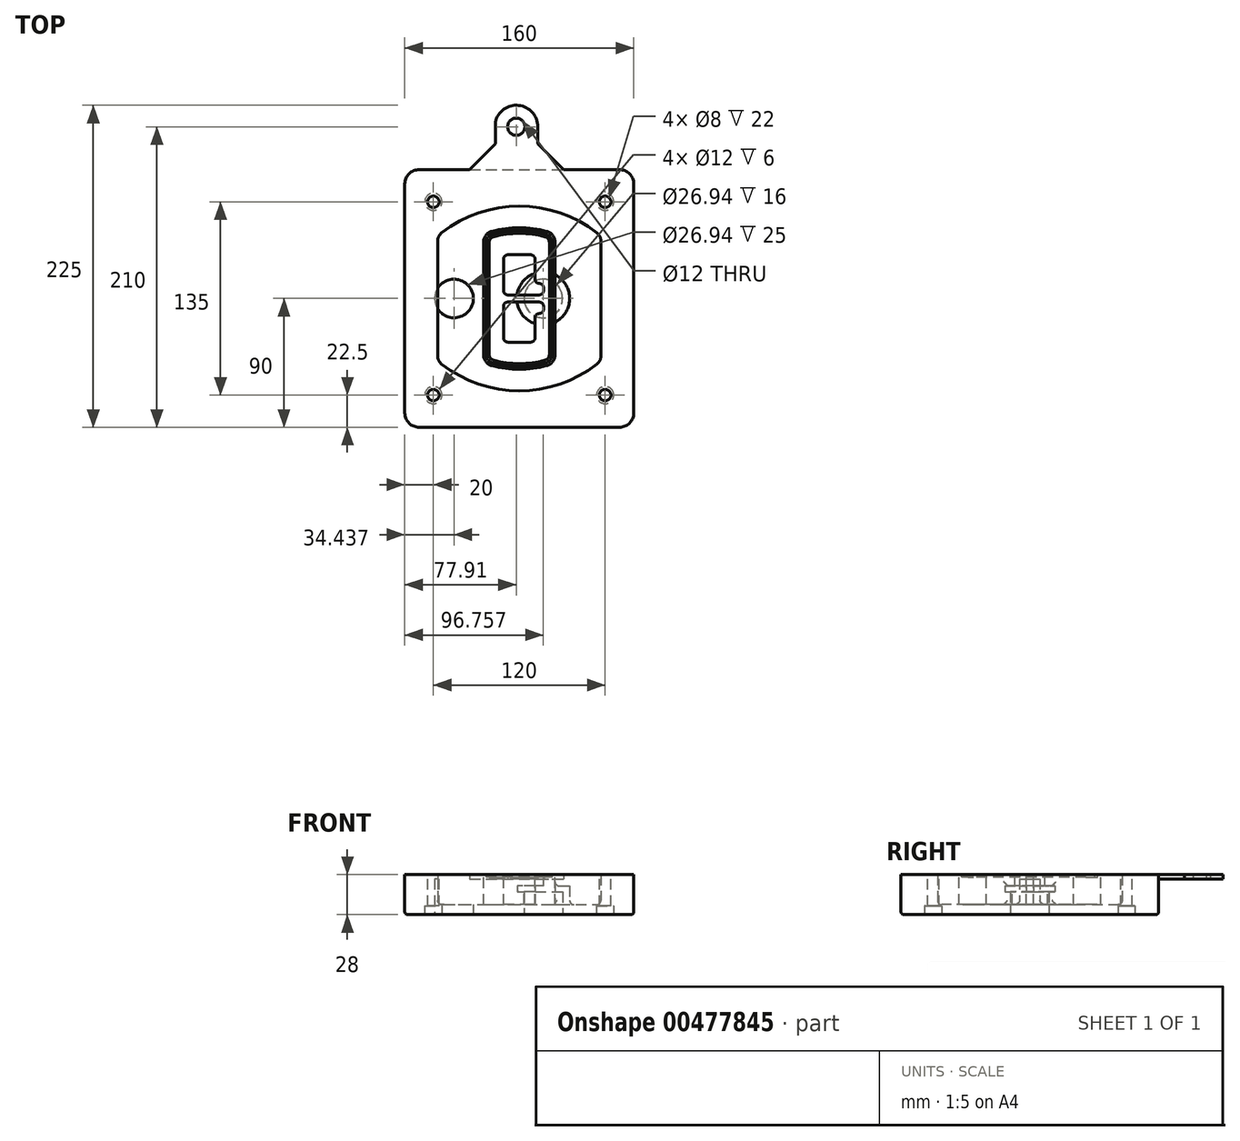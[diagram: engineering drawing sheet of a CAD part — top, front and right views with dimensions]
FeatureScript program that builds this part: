
annotation { "Feature Type Name" : "Feature", "Feature Type Description" : "" }
export const myFeature = defineFeature(function(context is Context, id is Id, definition is map)
    precondition{}
    {
        {
            var Q0;
            Q0=qCreatedBy(makeId("Top.planeOp"),FACE);
            var sketch = newSketch(context, id + "F0", { "sketchPlane" : qUnion([Q0])});
            skPoint(sketch, "E0.rect.middle", {"position": v(0, 0) * mm});
            skLineSegment(sketch, "E1.bottom", {"start": v(-70, -90) * mm, "end": v(70, -90) * mm});
            skLineSegment(sketch, "E1.top", {"start": v(-70, 90) * mm, "end": v(70, 90) * mm});
            skLineSegment(sketch, "E1.left", {"start": v(-80, -80) * mm, "end": v(-80, 80) * mm});
            skLineSegment(sketch, "E1.right", {"start": v(80, -80) * mm, "end": v(80, 80) * mm});
            skLineSegment(sketch, "E2", {"start": v(-80, 90) * mm, "end": v(80, -90) * mm, "construction": true});
            skLineSegment(sketch, "E3", {"start": v(80, 90) * mm, "end": v(-80, -90) * mm, "construction": true});
            skCircle(sketch, "E4", {"center": v(-60, 67.5) * mm, "radius": 4 * mm});
            skCircle(sketch, "E5", {"center": v(60, 67.5) * mm, "radius": 4 * mm});
            skCircle(sketch, "E6", {"center": v(60, -67.5) * mm, "radius": 4 * mm});
            skCircle(sketch, "E7", {"center": v(-60, -67.5) * mm, "radius": 4 * mm});
            skLineSegment(sketch, "E8", {"start": v(-60, 67.5) * mm, "end": v(60, 67.5) * mm, "construction": true});
            skLineSegment(sketch, "E9", {"start": v(60, 67.5) * mm, "end": v(60, -67.5) * mm, "construction": true});
            skLineSegment(sketch, "E10", {"start": v(60, -67.5) * mm, "end": v(-60, -67.5) * mm, "construction": true});
            skLineSegment(sketch, "E11", {"start": v(-60, -67.5) * mm, "end": v(-60, 67.5) * mm, "construction": true});
            skLineSegment(sketch, "E12", {"start": v(-60, 40.3) * mm, "end": v(-60, -40.3) * mm});
            skLineSegment(sketch, "E13", {"start": v(60, 40.3) * mm, "end": v(60, -40.3) * mm});
            skArc(sketch, "E14", {"start": v(56.15, 48.18) * mm, "mid": v(0, 67.5) * mm, "end": v(-56.15, 48.18) * mm});
            skArc(sketch, "E15", {"start": v(-56.15, -48.18) * mm, "mid": v(0, -67.5) * mm, "end": v(56.15, -48.18) * mm});
            skLineSegment(sketch, "E16", {"start": v(-60, 0) * mm, "end": v(60, 0) * mm, "construction": true});
            skPoint(sketch, "E17.visualSharp", {"position": v(-60, -45) * mm});
            skArc(sketch, "E17.filletArc", {"start": v(-60, -40.3) * mm, "mid": v(-58.99, -44.68) * mm, "end": v(-56.15, -48.18) * mm});
            skPoint(sketch, "E18.visualSharp", {"position": v(-60, 45) * mm});
            skArc(sketch, "E18.filletArc", {"start": v(-56.15, 48.18) * mm, "mid": v(-58.99, 44.68) * mm, "end": v(-60, 40.3) * mm});
            skPoint(sketch, "E19.visualSharp", {"position": v(60, 45) * mm});
            skArc(sketch, "E19.filletArc", {"start": v(60, 40.3) * mm, "mid": v(58.99, 44.68) * mm, "end": v(56.15, 48.18) * mm});
            skPoint(sketch, "E20.visualSharp", {"position": v(60, -45) * mm});
            skArc(sketch, "E20.filletArc", {"start": v(56.15, -48.18) * mm, "mid": v(58.99, -44.68) * mm, "end": v(60, -40.3) * mm});
            skPoint(sketch, "E21.visualSharp", {"position": v(-80, 90) * mm});
            skArc(sketch, "E21.filletArc", {"start": v(-70, 90) * mm, "mid": v(-77.07, 87.07) * mm, "end": v(-80, 80) * mm});
            skPoint(sketch, "E22.visualSharp", {"position": v(80, 90) * mm});
            skArc(sketch, "E22.filletArc", {"start": v(80, 80) * mm, "mid": v(77.07, 87.07) * mm, "end": v(70, 90) * mm});
            skPoint(sketch, "E23.visualSharp", {"position": v(80, -90) * mm});
            skArc(sketch, "E23.filletArc", {"start": v(70, -90) * mm, "mid": v(77.07, -87.07) * mm, "end": v(80, -80) * mm});
            skPoint(sketch, "E24.visualSharp", {"position": v(-80, -90) * mm});
            skArc(sketch, "E24.filletArc", {"start": v(-80, -80) * mm, "mid": v(-77.07, -87.07) * mm, "end": v(-70, -90) * mm});
            skArc(sketch, "E25.0", {"start": v(57, 40.3) * mm, "mid": v(56.3, 43.36) * mm, "end": v(54.3, 45.81) * mm});
            skLineSegment(sketch, "E25.1", {"start": v(57, 40.3) * mm, "end": v(57, -40.3) * mm});
            skArc(sketch, "E25.2", {"start": v(54.3, -45.81) * mm, "mid": v(56.3, -43.36) * mm, "end": v(57, -40.3) * mm});
            skArc(sketch, "E25.3", {"start": v(-54.3, -45.81) * mm, "mid": v(0, -64.5) * mm, "end": v(54.3, -45.81) * mm});
            skArc(sketch, "E25.4", {"start": v(-57, -40.3) * mm, "mid": v(-56.3, -43.36) * mm, "end": v(-54.3, -45.81) * mm});
            skArc(sketch, "E25.5", {"start": v(54.3, 45.81) * mm, "mid": v(0, 64.5) * mm, "end": v(-54.3, 45.81) * mm});
            skLineSegment(sketch, "E25.6", {"start": v(-57, 40.3) * mm, "end": v(-57, -40.3) * mm});
            skArc(sketch, "E25.7", {"start": v(-54.3, 45.81) * mm, "mid": v(-56.3, 43.36) * mm, "end": v(-57, 40.3) * mm});
            skArc(sketch, "E26.0", {"start": v(-58.62, 51.33) * mm, "mid": v(-62.58, 46.43) * mm, "end": v(-64, 40.3) * mm});
            skArc(sketch, "E26.1", {"start": v(58.62, 51.33) * mm, "mid": v(0, 71.5) * mm, "end": v(-58.62, 51.33) * mm});
            skArc(sketch, "E26.2", {"start": v(64, 40.3) * mm, "mid": v(62.58, 46.43) * mm, "end": v(58.62, 51.33) * mm});
            skLineSegment(sketch, "E26.3", {"start": v(64, 40.3) * mm, "end": v(64, -40.3) * mm});
            skArc(sketch, "E26.4", {"start": v(58.62, -51.33) * mm, "mid": v(62.58, -46.43) * mm, "end": v(64, -40.3) * mm});
            skLineSegment(sketch, "E26.5", {"start": v(-64, 40.3) * mm, "end": v(-64, -40.3) * mm});
            skArc(sketch, "E26.6", {"start": v(-58.62, -51.33) * mm, "mid": v(0, -71.5) * mm, "end": v(58.62, -51.33) * mm});
            skArc(sketch, "E26.7", {"start": v(-64, -40.3) * mm, "mid": v(-62.58, -46.43) * mm, "end": v(-58.62, -51.33) * mm});
            skSolve(sketch);
        }
        {
            var Q0;
            Q0=makeQuery(id+"F0.imprint","IMPRINT",FACE,{"disambiguationData":[TD([[makeQuery(id+"F0.imprint","IMPRINT",EDGE,{"derivedFrom":sQuery(id+"F0.wireOp",EDGE,"E1.bottom")}),1.0]])]});
            var Q1;
            Q1=makeQuery(id+"F0.imprint","IMPRINT",FACE,{"disambiguationData":[TD([[makeQuery(id+"F0.imprint","IMPRINT",EDGE,{"derivedFrom":sQuery(id+"F0.wireOp",EDGE,"E12")}),1.0]])]});
            var Q2;
            Q2=makeQuery(id+"F0.imprint","IMPRINT",FACE,{"disambiguationData":[TD([[makeQuery(id+"F0.imprint","IMPRINT",EDGE,{"derivedFrom":sQuery(id+"F0.wireOp",EDGE,"E25.0")}),1.0]])]});
            var Q3;
            Q3=makeQuery(id+"F0.imprint","IMPRINT",FACE,{"disambiguationData":[TD([[makeQuery(id+"F0.imprint","IMPRINT",EDGE,{"derivedFrom":sQuery(id+"F0.wireOp",EDGE,"E12")}),-1.0]])]});
            extrude(context, id + "F1", {"entities" : qUnion([Q0, Q1, Q2, Q3]), "oppositeDirection" : true, "depth" : 25 * mm});
        }
        {
            var Q0;
            Q0=makeQuery(id+"F0.imprint","IMPRINT",FACE,{"disambiguationData":[TD([[makeQuery(id+"F0.imprint","IMPRINT",EDGE,{"derivedFrom":sQuery(id+"F0.wireOp",EDGE,"E12")}),1.0]])]});
            extrude(context, id + "F2", {"entities" : qUnion([Q0]), "operationType" : NewBodyOperationType.ADD, "depth" : 3 * mm});
        }
        {
            var Q0;
            Q0=makeQuery(id+"F0.imprint","IMPRINT",FACE,{"disambiguationData":[TD([[makeQuery(id+"F0.imprint","IMPRINT",EDGE,{"derivedFrom":sQuery(id+"F0.wireOp",EDGE,"E25.0")}),1.0]])]});
            extrude(context, id + "F3", {"entities" : qUnion([Q0]), "operationType" : NewBodyOperationType.REMOVE, "oppositeDirection" : true, "depth" : 18 * mm});
        }
        {
            var Q0;
            Q0=makeQuery(id+"F2.opExtrude","CAP_FACE",FACE,{"disambiguationData":[OSD([sQuery(id+"F0.wireOp",EDGE,"E12"),sQuery(id+"F0.wireOp",EDGE,"E13"),sQuery(id+"F0.wireOp",EDGE,"E14"),sQuery(id+"F0.wireOp",EDGE,"E15"),sQuery(id+"F0.wireOp",EDGE,"E17.filletArc"),sQuery(id+"F0.wireOp",EDGE,"E18.filletArc"),sQuery(id+"F0.wireOp",EDGE,"E19.filletArc"),sQuery(id+"F0.wireOp",EDGE,"E20.filletArc"),sQuery(id+"F0.wireOp",EDGE,"E25.0"),sQuery(id+"F0.wireOp",EDGE,"E25.1"),sQuery(id+"F0.wireOp",EDGE,"E25.2"),sQuery(id+"F0.wireOp",EDGE,"E25.3"),sQuery(id+"F0.wireOp",EDGE,"E25.4"),sQuery(id+"F0.wireOp",EDGE,"E25.5"),sQuery(id+"F0.wireOp",EDGE,"E25.6"),sQuery(id+"F0.wireOp",EDGE,"E25.7")])],"isStart":false});
            var sketch = newSketch(context, id + "F4", { "sketchPlane" : qUnion([Q0])});
            skArc(sketch, "E27.0", {"start": v(-19.08, -46.97) * mm, "mid": v(0, -49.5) * mm, "end": v(19.08, -46.97) * mm});
            skArc(sketch, "E28.0", {"start": v(19.08, 46.97) * mm, "mid": v(0, 49.5) * mm, "end": v(-19.08, 46.97) * mm});
            skLineSegment(sketch, "E29", {"start": v(-25, 39.25) * mm, "end": v(-25, -39.25) * mm});
            skLineSegment(sketch, "E30", {"start": v(25, 39.25) * mm, "end": v(25, -39.25) * mm});
            skLineSegment(sketch, "E31", {"start": v(-25, 45.1) * mm, "end": v(25, 45.1) * mm, "construction": true});
            skLineSegment(sketch, "E32", {"start": v(-25, -45.1) * mm, "end": v(25, -45.1) * mm, "construction": true});
            skPoint(sketch, "E33.visualSharp", {"position": v(-25, 45.1) * mm});
            skArc(sketch, "E33.filletArc", {"start": v(-19.08, 46.97) * mm, "mid": v(-23.35, 44.11) * mm, "end": v(-25, 39.25) * mm});
            skPoint(sketch, "E34.visualSharp", {"position": v(25, 45.1) * mm});
            skArc(sketch, "E34.filletArc", {"start": v(25, 39.25) * mm, "mid": v(23.35, 44.11) * mm, "end": v(19.08, 46.97) * mm});
            skPoint(sketch, "E35.visualSharp", {"position": v(25, -45.1) * mm});
            skArc(sketch, "E35.filletArc", {"start": v(19.08, -46.97) * mm, "mid": v(23.35, -44.11) * mm, "end": v(25, -39.25) * mm});
            skPoint(sketch, "E36.visualSharp", {"position": v(-25, -45.1) * mm});
            skArc(sketch, "E36.filletArc", {"start": v(-25, -39.25) * mm, "mid": v(-23.35, -44.11) * mm, "end": v(-19.08, -46.97) * mm});
            skArc(sketch, "E37.0", {"start": v(54.3, 45.81) * mm, "mid": v(0, 64.5) * mm, "end": v(-54.3, 45.81) * mm});
            skArc(sketch, "E37.1", {"start": v(-54.3, 45.81) * mm, "mid": v(-56.3, 43.36) * mm, "end": v(-57, 40.3) * mm});
            skLineSegment(sketch, "E37.2", {"start": v(-57, 40.3) * mm, "end": v(-57, -40.3) * mm});
            skArc(sketch, "E37.3", {"start": v(-57, -40.3) * mm, "mid": v(-56.3, -43.36) * mm, "end": v(-54.3, -45.81) * mm});
            skArc(sketch, "E37.4", {"start": v(-54.3, -45.81) * mm, "mid": v(0, -64.5) * mm, "end": v(54.3, -45.81) * mm});
            skArc(sketch, "E37.5", {"start": v(54.3, -45.81) * mm, "mid": v(56.3, -43.36) * mm, "end": v(57, -40.3) * mm});
            skLineSegment(sketch, "E37.6", {"start": v(57, 40.3) * mm, "end": v(57, -40.3) * mm});
            skArc(sketch, "E37.7", {"start": v(57, 40.3) * mm, "mid": v(56.3, 43.36) * mm, "end": v(54.3, 45.81) * mm});
            skLineSegment(sketch, "E38.0", {"start": v(23, 39.25) * mm, "end": v(23, -39.25) * mm});
            skArc(sketch, "E38.1", {"start": v(18.56, -45.04) * mm, "mid": v(21.76, -42.9) * mm, "end": v(23, -39.25) * mm});
            skArc(sketch, "E38.2", {"start": v(-18.56, -45.04) * mm, "mid": v(0, -47.5) * mm, "end": v(18.56, -45.04) * mm});
            skArc(sketch, "E38.3", {"start": v(-23, -39.25) * mm, "mid": v(-21.76, -42.9) * mm, "end": v(-18.56, -45.04) * mm});
            skLineSegment(sketch, "E38.4", {"start": v(-23, 39.25) * mm, "end": v(-23, -39.25) * mm});
            skArc(sketch, "E38.5", {"start": v(23, 39.25) * mm, "mid": v(21.76, 42.9) * mm, "end": v(18.56, 45.04) * mm});
            skArc(sketch, "E38.6", {"start": v(-18.56, 45.04) * mm, "mid": v(-21.76, 42.9) * mm, "end": v(-23, 39.25) * mm});
            skArc(sketch, "E38.7", {"start": v(18.56, 45.04) * mm, "mid": v(0, 47.5) * mm, "end": v(-18.56, 45.04) * mm});
            skArc(sketch, "E39.0", {"start": v(21, 39.25) * mm, "mid": v(20.18, 41.68) * mm, "end": v(18.04, 43.1) * mm});
            skLineSegment(sketch, "E39.1", {"start": v(21, 39.25) * mm, "end": v(21, -39.25) * mm});
            skArc(sketch, "E39.2", {"start": v(18.04, -43.1) * mm, "mid": v(20.18, -41.68) * mm, "end": v(21, -39.25) * mm});
            skArc(sketch, "E39.3", {"start": v(-18.04, -43.1) * mm, "mid": v(0, -45.5) * mm, "end": v(18.04, -43.1) * mm});
            skArc(sketch, "E39.4", {"start": v(-21, -39.25) * mm, "mid": v(-20.18, -41.68) * mm, "end": v(-18.04, -43.1) * mm});
            skArc(sketch, "E39.5", {"start": v(18.04, 43.1) * mm, "mid": v(0, 45.5) * mm, "end": v(-18.04, 43.1) * mm});
            skLineSegment(sketch, "E39.6", {"start": v(-21, 39.25) * mm, "end": v(-21, -39.25) * mm});
            skArc(sketch, "E39.7", {"start": v(-18.04, 43.1) * mm, "mid": v(-20.18, 41.68) * mm, "end": v(-21, 39.25) * mm});
            skLineSegment(sketch, "E40", {"start": v(-25, 0) * mm, "end": v(25, 0) * mm, "construction": true});
            skLineSegment(sketch, "E41", {"start": v(-11, 5.5) * mm, "end": v(-11, 27.5) * mm});
            skLineSegment(sketch, "E42", {"start": v(-8, 30.5) * mm, "end": v(8, 30.5) * mm});
            skLineSegment(sketch, "E43", {"start": v(11, 27.5) * mm, "end": v(11, 13.5) * mm});
            skLineSegment(sketch, "E44", {"start": v(14, 10.5) * mm, "end": v(14, 10.5) * mm});
            skLineSegment(sketch, "E45", {"start": v(17, 7.5) * mm, "end": v(17, 5.5) * mm});
            skLineSegment(sketch, "E46", {"start": v(14, 2.5) * mm, "end": v(-8, 2.5) * mm});
            skPoint(sketch, "E47.visualSharp", {"position": v(-11, 30.5) * mm});
            skArc(sketch, "E47.filletArc", {"start": v(-8, 30.5) * mm, "mid": v(-10.12, 29.62) * mm, "end": v(-11, 27.5) * mm});
            skPoint(sketch, "E48.visualSharp", {"position": v(11, 30.5) * mm});
            skArc(sketch, "E48.filletArc", {"start": v(11, 27.5) * mm, "mid": v(10.12, 29.62) * mm, "end": v(8, 30.5) * mm});
            skPoint(sketch, "E49.visualSharp", {"position": v(11, 10.5) * mm});
            skArc(sketch, "E49.filletArc", {"start": v(11, 13.5) * mm, "mid": v(11.88, 11.38) * mm, "end": v(14, 10.5) * mm});
            skPoint(sketch, "E50.visualSharp", {"position": v(17, 10.5) * mm});
            skArc(sketch, "E50.filletArc", {"start": v(17, 7.5) * mm, "mid": v(16.12, 9.62) * mm, "end": v(14, 10.5) * mm});
            skPoint(sketch, "E51.visualSharp", {"position": v(17, 2.5) * mm});
            skArc(sketch, "E51.filletArc", {"start": v(14, 2.5) * mm, "mid": v(16.12, 3.38) * mm, "end": v(17, 5.5) * mm});
            skPoint(sketch, "E52.visualSharp", {"position": v(-11, 2.5) * mm});
            skArc(sketch, "E52.filletArc", {"start": v(-11, 5.5) * mm, "mid": v(-10.12, 3.38) * mm, "end": v(-8, 2.5) * mm});
            skLineSegment(sketch, "E53.0.MirrorCS", {"start": v(14, -2.5) * mm, "end": v(-8, -2.5) * mm});
            skArc(sketch, "E54.0.MirrorCS", {"start": v(-11, -5.5) * mm, "mid": v(-10.12, -3.38) * mm, "end": v(-8, -2.5) * mm});
            skLineSegment(sketch, "E55.0.MirrorCS", {"start": v(-11, -5.5) * mm, "end": v(-11, -27.5) * mm});
            skArc(sketch, "E56.0.MirrorCS", {"start": v(-8, -30.5) * mm, "mid": v(-10.12, -29.62) * mm, "end": v(-11, -27.5) * mm});
            skLineSegment(sketch, "E57.0.MirrorCS", {"start": v(-8, -30.5) * mm, "end": v(8, -30.5) * mm});
            skArc(sketch, "E58.0.MirrorCS", {"start": v(11, -27.5) * mm, "mid": v(10.12, -29.62) * mm, "end": v(8, -30.5) * mm});
            skLineSegment(sketch, "E59.0.MirrorCS", {"start": v(11, -27.5) * mm, "end": v(11, -13.5) * mm});
            skArc(sketch, "E60.0.MirrorCS", {"start": v(11, -13.5) * mm, "mid": v(11.88, -11.38) * mm, "end": v(14, -10.5) * mm});
            skArc(sketch, "E61.0.MirrorCS", {"start": v(17, -7.5) * mm, "mid": v(16.12, -9.62) * mm, "end": v(14, -10.5) * mm});
            skLineSegment(sketch, "E62.0.MirrorCS", {"start": v(17, -7.5) * mm, "end": v(17, -5.5) * mm});
            skArc(sketch, "E63.0.MirrorCS", {"start": v(14, -2.5) * mm, "mid": v(16.12, -3.38) * mm, "end": v(17, -5.5) * mm});
            skSolve(sketch);
        }
        {
            var Q0;
            Q0=makeQuery(id+"F4.imprint","IMPRINT",FACE,{"disambiguationData":[TD([[makeQuery(id+"F4.imprint","IMPRINT",EDGE,{"derivedFrom":sQuery(id+"F4.wireOp",EDGE,"E27.0")}),1.0]])]});
            var Q1;
            Q1=makeQuery(id+"F4.imprint","IMPRINT",FACE,{"disambiguationData":[TD([[makeQuery(id+"F4.imprint","IMPRINT",EDGE,{"derivedFrom":sQuery(id+"F4.wireOp",EDGE,"E38.0")}),-1.0]])]});
            var Q2;
            Q2=makeQuery(id+"F4.imprint","IMPRINT",FACE,{"disambiguationData":[TD([[makeQuery(id+"F4.imprint","IMPRINT",EDGE,{"derivedFrom":sQuery(id+"F4.wireOp",EDGE,"E39.0")}),1.0]])]});
            extrude(context, id + "F5", {"entities" : qUnion([Q0, Q1, Q2]), "operationType" : NewBodyOperationType.ADD, "endBound" : BoundingType.UP_TO_NEXT, "oppositeDirection" : true, "depth" : 25 * mm});
        }
        {
            var Q0;
            Q0=makeQuery(id+"F4.imprint","IMPRINT",FACE,{"disambiguationData":[TD([[makeQuery(id+"F4.imprint","IMPRINT",EDGE,{"derivedFrom":sQuery(id+"F4.wireOp",EDGE,"E38.0")}),-1.0]])]});
            extrude(context, id + "F6", {"entities" : qUnion([Q0]), "operationType" : NewBodyOperationType.REMOVE, "oppositeDirection" : true, "depth" : 2 * mm});
        }
        {
            var Q0;
            Q0=makeQuery(id+"F1.opExtrude","CAP_FACE",FACE,{"disambiguationData":[OSD([sQuery(id+"F0.wireOp",EDGE,"E1.bottom"),sQuery(id+"F0.wireOp",EDGE,"E1.top"),sQuery(id+"F0.wireOp",EDGE,"E1.left"),sQuery(id+"F0.wireOp",EDGE,"E1.right"),sQuery(id+"F0.wireOp",EDGE,"E4"),sQuery(id+"F0.wireOp",EDGE,"E5"),sQuery(id+"F0.wireOp",EDGE,"E6"),sQuery(id+"F0.wireOp",EDGE,"E7"),sQuery(id+"F0.wireOp",EDGE,"E21.filletArc"),sQuery(id+"F0.wireOp",EDGE,"E22.filletArc"),sQuery(id+"F0.wireOp",EDGE,"E23.filletArc"),sQuery(id+"F0.wireOp",EDGE,"E24.filletArc")])],"isStart":false});
            var sketch = newSketch(context, id + "F7", { "sketchPlane" : qUnion([Q0])});
            skCircle(sketch, "E64", {"center": v(16.76, 0) * mm, "radius": 13.47 * mm});
            skCircle(sketch, "E65", {"center": v(-45.56, 0) * mm, "radius": 13.47 * mm});
            skLineSegment(sketch, "E66", {"start": v(80, 0) * mm, "end": v(-80, 0) * mm});
            skCircle(sketch, "E67", {"center": v(16.76, 0) * mm, "radius": 18.47 * mm});
            skCircle(sketch, "E68", {"center": v(60, -67.5) * mm, "radius": 6 * mm});
            skCircle(sketch, "E69", {"center": v(-60, -67.5) * mm, "radius": 6 * mm});
            skCircle(sketch, "E70", {"center": v(-60, 67.5) * mm, "radius": 6 * mm});
            skCircle(sketch, "E71", {"center": v(60, 67.5) * mm, "radius": 6 * mm});
            skSolve(sketch);
        }
        {
            var Q0;
            {var subQ1=sQuery(id+"F7.wireOp",EDGE,"E66");var subQ4=sQuery(id+"F7.wireOp",EDGE,"E64");var subQ6=makeQuery(id+"F7.imprint","INTERSECT",VERTEX,{"disambiguationData":[OD(0.0)],"derivedFrom":[subQ4,subQ1]});Q0=makeQuery(id+"F7.imprint","IMPRINT",FACE,{"disambiguationData":[TD([[makeQuery(id+"F7.imprint","IMPRINT",EDGE,{"disambiguationData":[TD([[subQ6,-1.0]])],"derivedFrom":subQ4}),-1.0]])]});}
            var Q1;
            {var subQ0=sQuery(id+"F7.wireOp",EDGE,"E66");var subQ1=sQuery(id+"F7.wireOp",EDGE,"E64");var subQ3=makeQuery(id+"F7.imprint","INTERSECT",VERTEX,{"disambiguationData":[OD(0.0)],"derivedFrom":[subQ1,subQ0]});Q1=makeQuery(id+"F7.imprint","IMPRINT",FACE,{"disambiguationData":[TD([[makeQuery(id+"F7.imprint","IMPRINT",EDGE,{"disambiguationData":[TD([[subQ3,-1.0]])],"derivedFrom":subQ1}),1.0]])]});}
            var Q2;
            {var subQ0=sQuery(id+"F7.wireOp",EDGE,"E66");var subQ1=sQuery(id+"F7.wireOp",EDGE,"E64");var subQ3=makeQuery(id+"F7.imprint","INTERSECT",VERTEX,{"disambiguationData":[OD(0.0)],"derivedFrom":[subQ1,subQ0]});Q2=makeQuery(id+"F7.imprint","IMPRINT",FACE,{"disambiguationData":[TD([[makeQuery(id+"F7.imprint","IMPRINT",EDGE,{"disambiguationData":[TD([[subQ3,1.0]])],"derivedFrom":subQ1}),1.0]])]});}
            var Q3;
            {var subQ1=sQuery(id+"F7.wireOp",EDGE,"E66");var subQ4=sQuery(id+"F7.wireOp",EDGE,"E64");var subQ6=makeQuery(id+"F7.imprint","INTERSECT",VERTEX,{"disambiguationData":[OD(0.0)],"derivedFrom":[subQ4,subQ1]});Q3=makeQuery(id+"F7.imprint","IMPRINT",FACE,{"disambiguationData":[TD([[makeQuery(id+"F7.imprint","IMPRINT",EDGE,{"disambiguationData":[TD([[subQ6,1.0]])],"derivedFrom":subQ4}),-1.0]])]});}
            extrude(context, id + "F8", {"entities" : qUnion([Q0, Q1, Q2, Q3]), "operationType" : NewBodyOperationType.ADD, "oppositeDirection" : true, "depth" : 20 * mm});
        }
        {
            var Q0;
            {var subQ0=sQuery(id+"F7.wireOp",EDGE,"E66");var subQ1=sQuery(id+"F7.wireOp",EDGE,"E64");var subQ3=makeQuery(id+"F7.imprint","INTERSECT",VERTEX,{"disambiguationData":[OD(0.0)],"derivedFrom":[subQ1,subQ0]});Q0=makeQuery(id+"F7.imprint","IMPRINT",FACE,{"disambiguationData":[TD([[makeQuery(id+"F7.imprint","IMPRINT",EDGE,{"disambiguationData":[TD([[subQ3,-1.0]])],"derivedFrom":subQ1}),1.0]])]});}
            var Q1;
            {var subQ0=sQuery(id+"F7.wireOp",EDGE,"E66");var subQ1=sQuery(id+"F7.wireOp",EDGE,"E64");var subQ3=makeQuery(id+"F7.imprint","INTERSECT",VERTEX,{"disambiguationData":[OD(0.0)],"derivedFrom":[subQ1,subQ0]});Q1=makeQuery(id+"F7.imprint","IMPRINT",FACE,{"disambiguationData":[TD([[makeQuery(id+"F7.imprint","IMPRINT",EDGE,{"disambiguationData":[TD([[subQ3,1.0]])],"derivedFrom":subQ1}),1.0]])]});}
            extrude(context, id + "F9", {"entities" : qUnion([Q0, Q1]), "operationType" : NewBodyOperationType.REMOVE, "oppositeDirection" : true, "depth" : 16 * mm});
        }
        {
            var Q0;
            {var subQ0=sQuery(id+"F7.wireOp",EDGE,"E66");var subQ1=sQuery(id+"F7.wireOp",EDGE,"E65");var subQ3=makeQuery(id+"F7.imprint","INTERSECT",VERTEX,{"disambiguationData":[OD(0.0)],"derivedFrom":[subQ1,subQ0]});Q0=makeQuery(id+"F7.imprint","IMPRINT",FACE,{"disambiguationData":[TD([[makeQuery(id+"F7.imprint","IMPRINT",EDGE,{"disambiguationData":[TD([[subQ3,-1.0]])],"derivedFrom":subQ1}),1.0]])]});}
            var Q1;
            {var subQ0=sQuery(id+"F7.wireOp",EDGE,"E66");var subQ1=sQuery(id+"F7.wireOp",EDGE,"E65");var subQ3=makeQuery(id+"F7.imprint","INTERSECT",VERTEX,{"disambiguationData":[OD(0.0)],"derivedFrom":[subQ1,subQ0]});Q1=makeQuery(id+"F7.imprint","IMPRINT",FACE,{"disambiguationData":[TD([[makeQuery(id+"F7.imprint","IMPRINT",EDGE,{"disambiguationData":[TD([[subQ3,1.0]])],"derivedFrom":subQ1}),1.0]])]});}
            extrude(context, id + "F10", {"entities" : qUnion([Q0, Q1]), "operationType" : NewBodyOperationType.REMOVE, "oppositeDirection" : true, "depth" : 25 * mm});
        }
        {
            var Q0;
            Q0=makeQuery(id+"F7.imprint","IMPRINT",FACE,{"disambiguationData":[TD([[makeQuery(id+"F7.imprint","IMPRINT",EDGE,{"derivedFrom":sQuery(id+"F7.wireOp",EDGE,"E68")}),1.0]])]});
            var Q1;
            Q1=makeQuery(id+"F7.imprint","IMPRINT",FACE,{"disambiguationData":[TD([[makeQuery(id+"F7.imprint","IMPRINT",EDGE,{"derivedFrom":makeQuery(id+"F1.opExtrude","CAP_EDGE",EDGE,{"disambiguationData":[OSD([sQuery(id+"F0.wireOp",EDGE,"E5")])],"isStart":false})}),-1.0]])]});
            var Q2;
            Q2=makeQuery(id+"F7.imprint","IMPRINT",FACE,{"disambiguationData":[TD([[makeQuery(id+"F7.imprint","IMPRINT",EDGE,{"derivedFrom":sQuery(id+"F7.wireOp",EDGE,"E69")}),1.0]])]});
            var Q3;
            Q3=makeQuery(id+"F7.imprint","IMPRINT",FACE,{"disambiguationData":[TD([[makeQuery(id+"F7.imprint","IMPRINT",EDGE,{"derivedFrom":makeQuery(id+"F1.opExtrude","CAP_EDGE",EDGE,{"disambiguationData":[OSD([sQuery(id+"F0.wireOp",EDGE,"E4")])],"isStart":false})}),-1.0]])]});
            var Q4;
            Q4=makeQuery(id+"F7.imprint","IMPRINT",FACE,{"disambiguationData":[TD([[makeQuery(id+"F7.imprint","IMPRINT",EDGE,{"derivedFrom":sQuery(id+"F7.wireOp",EDGE,"E70")}),1.0]])]});
            var Q5;
            Q5=makeQuery(id+"F7.imprint","IMPRINT",FACE,{"disambiguationData":[TD([[makeQuery(id+"F7.imprint","IMPRINT",EDGE,{"derivedFrom":makeQuery(id+"F1.opExtrude","CAP_EDGE",EDGE,{"disambiguationData":[OSD([sQuery(id+"F0.wireOp",EDGE,"E7")])],"isStart":false})}),-1.0]])]});
            var Q6;
            Q6=makeQuery(id+"F7.imprint","IMPRINT",FACE,{"disambiguationData":[TD([[makeQuery(id+"F7.imprint","IMPRINT",EDGE,{"derivedFrom":sQuery(id+"F7.wireOp",EDGE,"E71")}),1.0]])]});
            var Q7;
            Q7=makeQuery(id+"F7.imprint","IMPRINT",FACE,{"disambiguationData":[TD([[makeQuery(id+"F7.imprint","IMPRINT",EDGE,{"derivedFrom":makeQuery(id+"F1.opExtrude","CAP_EDGE",EDGE,{"disambiguationData":[OSD([sQuery(id+"F0.wireOp",EDGE,"E6")])],"isStart":false})}),-1.0]])]});
            extrude(context, id + "F11", {"entities" : qUnion([Q0, Q1, Q2, Q3, Q4, Q5, Q6, Q7]), "operationType" : NewBodyOperationType.REMOVE, "oppositeDirection" : true, "depth" : 6 * mm});
        }
        {
            var Q0;
            Q0=makeQuery(id+"F9.boolean.opBoolean","COPY",FACE,{"derivedFrom":makeQuery(id+"F9.opExtrude","CAP_FACE",FACE,{"disambiguationData":[OSD([sQuery(id+"F7.wireOp",EDGE,"E64")])],"isStart":false})});
            var sketch = newSketch(context, id + "F12", { "sketchPlane" : qUnion([Q0])});
            skArc(sketch, "E72.0", {"start": v(11, 17.55) * mm, "mid": v(2.57, 11.82) * mm, "end": v(-1.54, 2.5) * mm});
            skArc(sketch, "E72.1", {"start": v(-1.54, -2.5) * mm, "mid": v(2.57, -11.82) * mm, "end": v(11, -17.55) * mm});
            skLineSegment(sketch, "E73", {"start": v(-1.54, -2.5) * mm, "end": v(14, -2.5) * mm});
            skLineSegment(sketch, "E74.0", {"start": v(14, 2.5) * mm, "end": v(-1.54, 2.5) * mm});
            skArc(sketch, "E74.1", {"start": v(14, 2.5) * mm, "mid": v(16.12, 3.38) * mm, "end": v(17, 5.5) * mm});
            skLineSegment(sketch, "E74.2", {"start": v(17, 7.5) * mm, "end": v(17, 5.5) * mm});
            skArc(sketch, "E74.3", {"start": v(17, 7.5) * mm, "mid": v(16.12, 9.62) * mm, "end": v(14, 10.5) * mm});
            skArc(sketch, "E74.4", {"start": v(11, 13.5) * mm, "mid": v(11.88, 11.38) * mm, "end": v(14, 10.5) * mm});
            skLineSegment(sketch, "E74.5", {"start": v(11, 17.55) * mm, "end": v(11, 13.5) * mm});
            skLineSegment(sketch, "E74.7", {"start": v(14, -2.5) * mm, "end": v(-1.54, -2.5) * mm});
            skArc(sketch, "E74.8", {"start": v(14, -2.5) * mm, "mid": v(16.12, -3.38) * mm, "end": v(17, -5.5) * mm});
            skLineSegment(sketch, "E74.9", {"start": v(17, -7.5) * mm, "end": v(17, -5.5) * mm});
            skArc(sketch, "E74.10", {"start": v(17, -7.5) * mm, "mid": v(16.12, -9.62) * mm, "end": v(14, -10.5) * mm});
            skArc(sketch, "E74.11", {"start": v(11, -13.5) * mm, "mid": v(11.88, -11.38) * mm, "end": v(14, -10.5) * mm});
            skLineSegment(sketch, "E74.12", {"start": v(11, -17.55) * mm, "end": v(11, -13.5) * mm});
            skPoint(sketch, "E75.orphan", {"position": v(11, -27.5) * mm});
            skPoint(sketch, "E76.orphan", {"position": v(-8, -2.5) * mm});
            skPoint(sketch, "E77.orphan", {"position": v(-8, 2.5) * mm});
            skPoint(sketch, "E78.orphan", {"position": v(11, 27.5) * mm});
            skSolve(sketch);
        }
        {
            var Q0;
            {var subQ7=sQuery(id+"F12.wireOp",EDGE,"E72.0");var subQ14=sQuery(id+"F12.wireOp",EDGE,"E72.1");var subQ16=sQuery(id+"F12.wireOp",EDGE,"E74.1");var subQ18=sQuery(id+"F12.wireOp",EDGE,"E74.8");Q0=qUnion([makeQuery(id+"F12.imprint","IMPRINT",FACE,{"disambiguationData":[TD([[makeQuery(id+"F12.imprint","IMPRINT",EDGE,{"derivedFrom":subQ7}),1.0]])]}),makeQuery(id+"F12.imprint","IMPRINT",FACE,{"disambiguationData":[TD([[makeQuery(id+"F12.imprint","IMPRINT",EDGE,{"derivedFrom":subQ14}),1.0]])]}),makeQuery(id+"F12.imprint","IMPRINT",FACE,{"disambiguationData":[TD([[makeQuery(id+"F12.imprint","IMPRINT",EDGE,{"derivedFrom":subQ16}),1.0]])]}),makeQuery(id+"F12.imprint","IMPRINT",FACE,{"disambiguationData":[TD([[makeQuery(id+"F12.imprint","IMPRINT",EDGE,{"derivedFrom":subQ18}),-1.0]])]})]);}
            var Q1;
            Q1=makeQuery(id+"F5.boolean.opBoolean","SPLIT",FACE,{"disambiguationData":[TD([makeQuery(id+"F5.opExtrude","SWEPT_FACE",FACE,{"disambiguationData":[OSD([sQuery(id+"F4.wireOp",EDGE,"E41")])]})])],"derivedFrom":makeQuery(id+"F3.boolean.opBoolean","COPY",FACE,{"derivedFrom":makeQuery(id+"F3.opExtrude","CAP_FACE",FACE,{"disambiguationData":[OSD([sQuery(id+"F0.wireOp",EDGE,"E25.0"),sQuery(id+"F0.wireOp",EDGE,"E25.1"),sQuery(id+"F0.wireOp",EDGE,"E25.2"),sQuery(id+"F0.wireOp",EDGE,"E25.3"),sQuery(id+"F0.wireOp",EDGE,"E25.4"),sQuery(id+"F0.wireOp",EDGE,"E25.5"),sQuery(id+"F0.wireOp",EDGE,"E25.6"),sQuery(id+"F0.wireOp",EDGE,"E25.7")])],"isStart":false})})});
            extrude(context, id + "F13", {"entities" : qUnion([Q0]), "operationType" : NewBodyOperationType.REMOVE, "endBound" : BoundingType.UP_TO_SURFACE, "endBoundEntityFace" : qUnion([Q1]), "depth" : 25 * mm});
        }
        {
            var Q0;
            Q0=makeQuery(id+"F3.boolean.opBoolean","COPY",EDGE,{"derivedFrom":makeQuery(id+"F3.opExtrude","CAP_EDGE",EDGE,{"disambiguationData":[OSD([sQuery(id+"F0.wireOp",EDGE,"E25.6")])],"isStart":false})});
            var Q1;
            Q1=makeQuery(id+"F8.boolean.opBoolean","INTERSECT",EDGE,{"derivedFrom":[makeQuery(id+"F5.opExtrude","SWEPT_FACE",FACE,{"disambiguationData":[OSD([sQuery(id+"F4.wireOp",EDGE,"E30")])]}),makeQuery(id+"F8.opExtrude","CAP_FACE",FACE,{"disambiguationData":[OSD([sQuery(id+"F7.wireOp",EDGE,"E67")])],"isStart":false})]});
            var Q2;
            Q2=makeQuery(id+"F8.boolean.opBoolean","INTERSECT",EDGE,{"disambiguationData":[OD(1.0)],"derivedFrom":[makeQuery(id+"F5.opExtrude","SWEPT_FACE",FACE,{"disambiguationData":[OSD([sQuery(id+"F4.wireOp",EDGE,"E30")])]}),makeQuery(id+"F8.opExtrude","SWEPT_FACE",FACE,{"disambiguationData":[OSD([sQuery(id+"F7.wireOp",EDGE,"E67")])]})]});
            var Q3;
            {var subQ0=sQuery(id+"F4.wireOp",EDGE,"E30");Q3=makeQuery(id+"F8.boolean.opBoolean","SPLIT",EDGE,{"disambiguationData":[TD([makeQuery(id+"F5.opExtrude","SWEPT_FACE",FACE,{"disambiguationData":[OSD([sQuery(id+"F4.wireOp",EDGE,"E35.filletArc")])]})])],"derivedFrom":makeQuery(id+"F5.opExtrude","CAP_EDGE",EDGE,{"disambiguationData":[OSD([subQ0])],"isStart":false})});}
            var Q4;
            {var subQ0=sQuery(id+"F0.wireOp",EDGE,"E25.7");var subQ1=sQuery(id+"F0.wireOp",EDGE,"E25.1");var subQ2=sQuery(id+"F0.wireOp",EDGE,"E25.6");var subQ3=sQuery(id+"F0.wireOp",EDGE,"E25.5");var subQ4=sQuery(id+"F0.wireOp",EDGE,"E25.4");var subQ5=sQuery(id+"F0.wireOp",EDGE,"E25.0");var subQ6=sQuery(id+"F0.wireOp",EDGE,"E25.2");var subQ7=sQuery(id+"F0.wireOp",EDGE,"E25.3");Q4=makeQuery(id+"F8.boolean.opBoolean","INTERSECT",EDGE,{"derivedFrom":[makeQuery(id+"F5.boolean.opBoolean","SPLIT",FACE,{"disambiguationData":[TD([makeQuery(id+"F2.opExtrude","SWEPT_FACE",FACE,{"disambiguationData":[OSD([subQ5])]})])],"derivedFrom":makeQuery(id+"F3.boolean.opBoolean","COPY",FACE,{"derivedFrom":makeQuery(id+"F3.opExtrude","CAP_FACE",FACE,{"disambiguationData":[OSD([subQ5,subQ1,subQ6,subQ7,subQ4,subQ3,subQ2,subQ0])],"isStart":false})})}),makeQuery(id+"F8.opExtrude","SWEPT_FACE",FACE,{"disambiguationData":[OSD([sQuery(id+"F7.wireOp",EDGE,"E67")])]})]});}
            var Q5;
            Q5=makeQuery(id+"F8.boolean.opBoolean","INTERSECT",EDGE,{"disambiguationData":[OD(0.0)],"derivedFrom":[makeQuery(id+"F5.opExtrude","SWEPT_FACE",FACE,{"disambiguationData":[OSD([sQuery(id+"F4.wireOp",EDGE,"E30")])]}),makeQuery(id+"F8.opExtrude","SWEPT_FACE",FACE,{"disambiguationData":[OSD([sQuery(id+"F7.wireOp",EDGE,"E67")])]})]});
            fillet(context, id + "F14", {"entities" : qUnion([Q0, Q1, Q2, Q3, Q4, Q5]), "radius" : 3 * mm, "tangentPropagation" : true, "allowEdgeOverflow" : false});
        }
        {
            var Q0;
            Q0=makeQuery(id+"F1.opExtrude","CAP_EDGE",EDGE,{"disambiguationData":[OSD([sQuery(id+"F0.wireOp",EDGE,"E1.bottom")])],"isStart":false});
            fillet(context, id + "F15", {"entities" : qUnion([Q0]), "radius" : 2 * mm, "tangentPropagation" : true, "allowEdgeOverflow" : false});
        }
        {
            var Q0;
            {var subQ0=sQuery(id+"F0.wireOp",EDGE,"E21.filletArc");var subQ1=sQuery(id+"F0.wireOp",EDGE,"E7");var subQ2=sQuery(id+"F0.wireOp",EDGE,"E6");var subQ3=sQuery(id+"F0.wireOp",EDGE,"E5");var subQ4=sQuery(id+"F0.wireOp",EDGE,"E4");var subQ5=sQuery(id+"F0.wireOp",EDGE,"E22.filletArc");var subQ6=sQuery(id+"F0.wireOp",EDGE,"E1.bottom");var subQ7=sQuery(id+"F0.wireOp",EDGE,"E1.right");var subQ8=sQuery(id+"F0.wireOp",EDGE,"E1.top");var subQ9=sQuery(id+"F0.wireOp",EDGE,"E1.left");var subQ10=sQuery(id+"F0.wireOp",EDGE,"E23.filletArc");var subQ11=sQuery(id+"F0.wireOp",EDGE,"E24.filletArc");Q0=makeQuery(id+"F2.boolean.opBoolean","SPLIT",FACE,{"disambiguationData":[TD([makeQuery(id+"F1.opExtrude","SWEPT_FACE",FACE,{"disambiguationData":[OSD([subQ6])]})])],"derivedFrom":makeQuery(id+"F1.opExtrude","CAP_FACE",FACE,{"disambiguationData":[OSD([subQ6,subQ8,subQ9,subQ7,subQ4,subQ3,subQ2,subQ1,subQ0,subQ5,subQ10,subQ11])],"isStart":true})});}
            var sketch = newSketch(context, id + "F16", { "sketchPlane" : qUnion([Q0])});
            skLineSegment(sketch, "E79.0.0", {"start": v(70, 90) * mm, "end": v(-70, 90) * mm});
            skArc(sketch, "E79.0.1", {"start": v(-70, 90) * mm, "mid": v(-77.07, 87.07) * mm, "end": v(-80, 80) * mm});
            skLineSegment(sketch, "E79.0.2", {"start": v(-80, 80) * mm, "end": v(-80, -80) * mm});
            skArc(sketch, "E79.0.3", {"start": v(-80, -80) * mm, "mid": v(-77.07, -87.07) * mm, "end": v(-70, -90) * mm});
            skLineSegment(sketch, "E79.0.4", {"start": v(-70, -90) * mm, "end": v(70, -90) * mm});
            skArc(sketch, "E79.0.5", {"start": v(70, -90) * mm, "mid": v(77.07, -87.07) * mm, "end": v(80, -80) * mm});
            skLineSegment(sketch, "E79.0.6", {"start": v(80, -80) * mm, "end": v(80, 80) * mm});
            skArc(sketch, "E79.0.7", {"start": v(80, 80) * mm, "mid": v(77.07, 87.07) * mm, "end": v(70, 90) * mm});
            skLineSegment(sketch, "E80", {"start": v(-34.72, 90) * mm, "end": v(-16.72, 108) * mm});
            skLineSegment(sketch, "E81", {"start": v(-16.72, 108) * mm, "end": v(-16.72, 123.3) * mm});
            skLineSegment(sketch, "E82", {"start": v(12.91, 108) * mm, "end": v(12.91, 120) * mm});
            skArc(sketch, "E83", {"start": v(12.91, 120) * mm, "mid": v(-0.43, 134.9) * mm, "end": v(-16.72, 123.3) * mm});
            skLineSegment(sketch, "E84", {"start": v(12.91, 108) * mm, "end": v(30.91, 90) * mm});
            skCircle(sketch, "E85", {"center": v(-2.09, 120) * mm, "radius": 6 * mm});
            skLineSegment(sketch, "E86", {"start": v(-2.09, 120) * mm, "end": v(-2.09, 90) * mm, "construction": true});
            skLineSegment(sketch, "E87", {"start": v(-80, 0) * mm, "end": v(80, 0) * mm, "construction": true});
            skLineSegment(sketch, "E88.MirrorCS", {"start": v(70, -90) * mm, "end": v(-70, -90) * mm});
            skArc(sketch, "E89.MirrorCS", {"start": v(12.91, -120) * mm, "mid": v(-0.43, -134.9) * mm, "end": v(-16.72, -123.3) * mm});
            skLineSegment(sketch, "E90.MirrorCS", {"start": v(-16.72, -108) * mm, "end": v(-16.72, -123.3) * mm});
            skCircle(sketch, "E91.MirrorC", {"center": v(-2.09, -120) * mm, "radius": 6 * mm});
            skLineSegment(sketch, "E92.MirrorCS", {"start": v(-2.09, -120) * mm, "end": v(-2.09, -90) * mm, "construction": true});
            skLineSegment(sketch, "E93.MirrorCS", {"start": v(-34.72, -90) * mm, "end": v(-16.72, -108) * mm});
            skLineSegment(sketch, "E94.MirrorCS", {"start": v(12.91, -108) * mm, "end": v(12.91, -120) * mm});
            skLineSegment(sketch, "E95.MirrorCS", {"start": v(12.91, -108) * mm, "end": v(30.91, -90) * mm});
            skSolve(sketch);
        }
        {
            var Q0;
            {var subQ0=sQuery(id+"F16.wireOp",EDGE,"E80");Q0=makeQuery(id+"F16.imprint","IMPRINT",FACE,{"disambiguationData":[TD([[makeQuery(id+"F16.imprint","IMPRINT",EDGE,{"derivedFrom":subQ0}),-1.0]])]});}
            var Q1;
            Q1=makeQuery(id+"F16.imprint","IMPRINT",FACE,{"disambiguationData":[TD([[makeQuery(id+"F16.imprint","IMPRINT",EDGE,{"derivedFrom":sQuery(id+"F16.wireOp",EDGE,"E89.MirrorCS")}),-1.0]])]});
            var Q2;
            {var subQ4=sQuery(id+"F16.wireOp",EDGE,"E79.0.1");Q2=makeQuery(id+"F16.imprint","IMPRINT",FACE,{"disambiguationData":[TD([[makeQuery(id+"F16.imprint","IMPRINT",EDGE,{"derivedFrom":subQ4}),1.0]])]});}
            var Q3;
            Q3=makeQuery(id+"F2.opExtrude","CAP_FACE",FACE,{"disambiguationData":[OSD([sQuery(id+"F0.wireOp",EDGE,"E12"),sQuery(id+"F0.wireOp",EDGE,"E13"),sQuery(id+"F0.wireOp",EDGE,"E14"),sQuery(id+"F0.wireOp",EDGE,"E15"),sQuery(id+"F0.wireOp",EDGE,"E17.filletArc"),sQuery(id+"F0.wireOp",EDGE,"E18.filletArc"),sQuery(id+"F0.wireOp",EDGE,"E19.filletArc"),sQuery(id+"F0.wireOp",EDGE,"E20.filletArc"),sQuery(id+"F0.wireOp",EDGE,"E25.0"),sQuery(id+"F0.wireOp",EDGE,"E25.1"),sQuery(id+"F0.wireOp",EDGE,"E25.2"),sQuery(id+"F0.wireOp",EDGE,"E25.3"),sQuery(id+"F0.wireOp",EDGE,"E25.4"),sQuery(id+"F0.wireOp",EDGE,"E25.5"),sQuery(id+"F0.wireOp",EDGE,"E25.6"),sQuery(id+"F0.wireOp",EDGE,"E25.7")])],"isStart":false});
            extrude(context, id + "F17", {"entities" : qUnion([Q0, Q1, Q2]), "operationType" : NewBodyOperationType.ADD, "endBound" : BoundingType.UP_TO_SURFACE, "endBoundEntityFace" : qUnion([Q3]), "depth" : 25 * mm});
        }
    });
